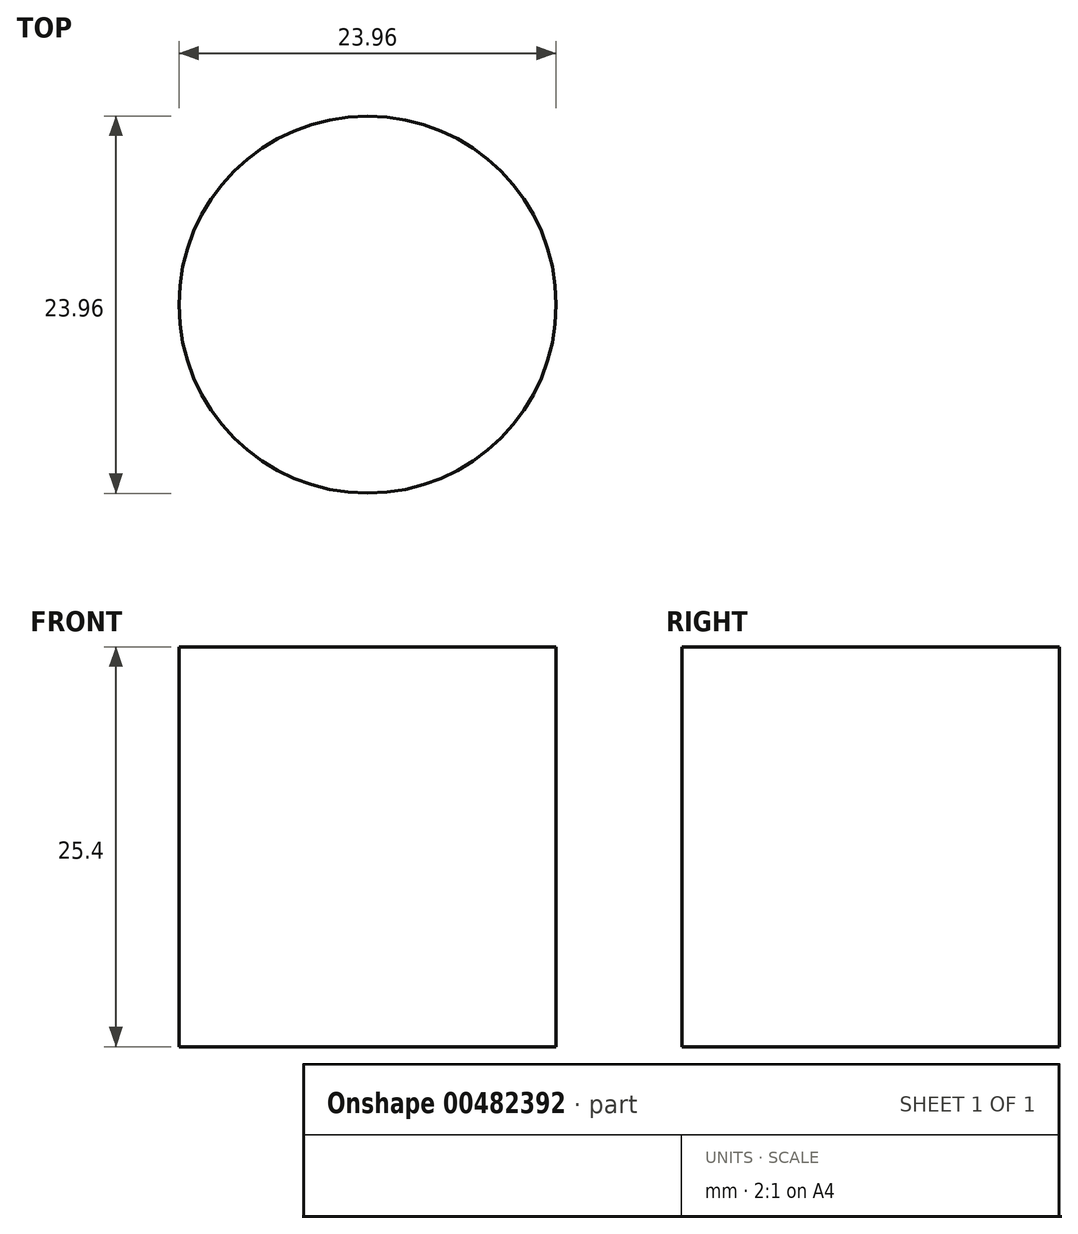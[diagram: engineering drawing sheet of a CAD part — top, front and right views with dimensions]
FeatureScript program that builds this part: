
annotation { "Feature Type Name" : "Feature", "Feature Type Description" : "" }
export const myFeature = defineFeature(function(context is Context, id is Id, definition is map)
    precondition{}
    {
        {
            var Q0;
            Q0=qCreatedBy(makeId("Top.planeOp"),FACE);
            var sketch = newSketch(context, id + "F0", { "sketchPlane" : qUnion([Q0])});
            skCircle(sketch, "E0", {"center": v(0, 0) * mm, "radius": 11.98 * mm});
            skSolve(sketch);
        }
        {
            var Q0;
            Q0=makeQuery(id+"F0.imprint","IMPRINT",FACE,{"disambiguationData":[TD([[makeQuery(id+"F0.imprint","IMPRINT",EDGE,{"derivedFrom":sQuery(id+"F0.wireOp",EDGE,"E0")}),1.0]])]});
            extrude(context, id + "F1", {"entities" : qUnion([Q0]), "depth" : 25.4 * mm});
        }
    });
